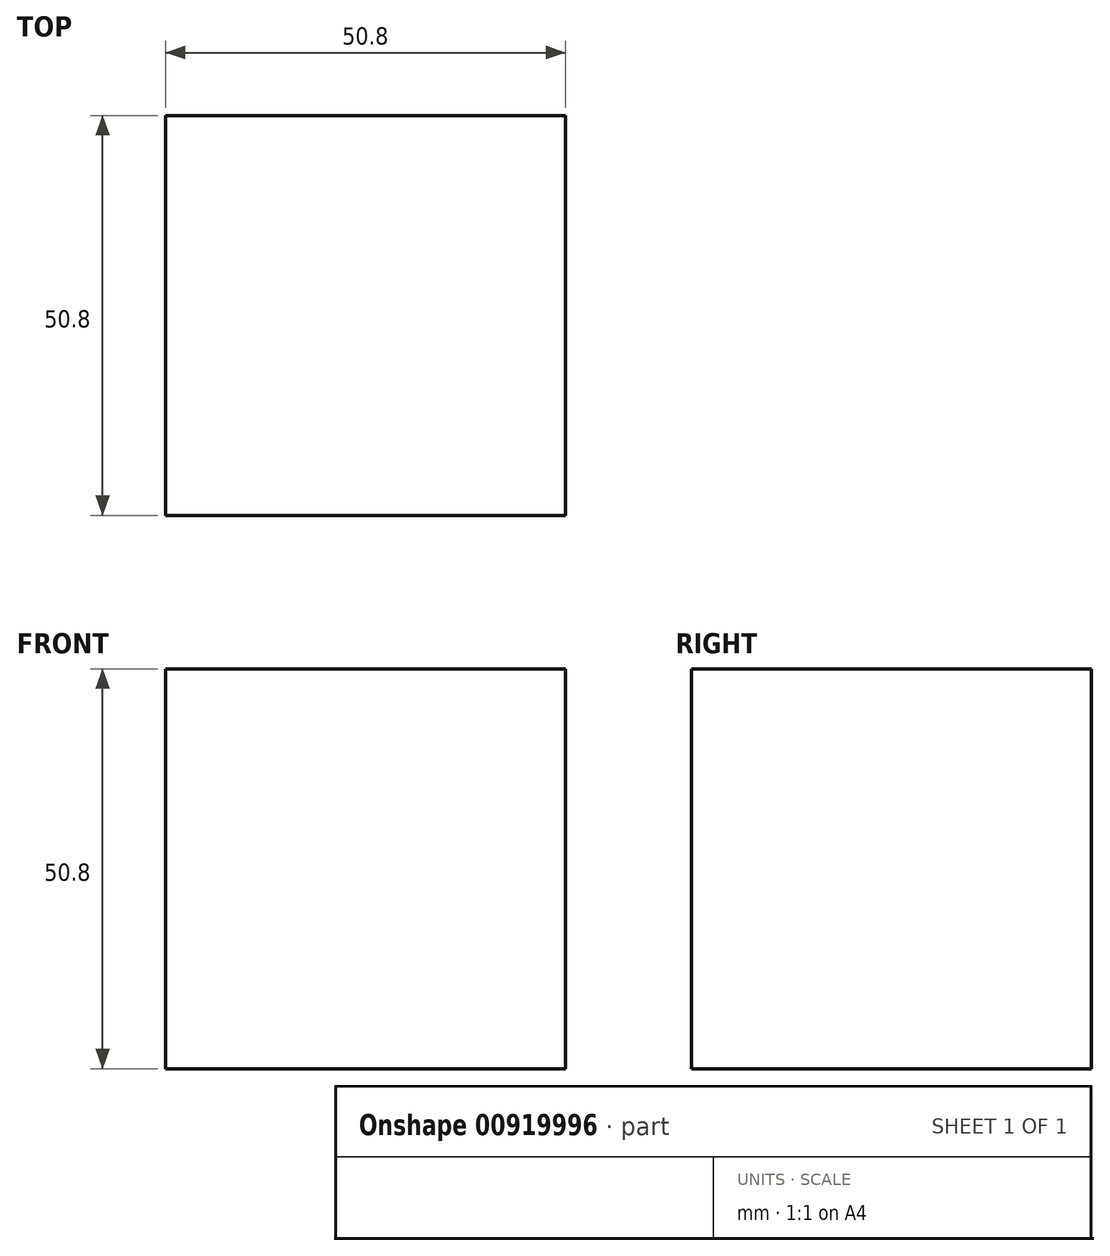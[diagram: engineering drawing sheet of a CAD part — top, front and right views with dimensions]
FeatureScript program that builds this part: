
annotation { "Feature Type Name" : "Feature", "Feature Type Description" : "" }
export const myFeature = defineFeature(function(context is Context, id is Id, definition is map)
    precondition{}
    {
        {
            var Q0;
            Q0=qCreatedBy(makeId("Top.planeOp"),FACE);
            var sketch = newSketch(context, id + "F0", { "sketchPlane" : qUnion([Q0])});
            skLineSegment(sketch, "E0.bottom", {"start": v(-23.76, 20.42) * mm, "end": v(27.04, 20.42) * mm});
            skLineSegment(sketch, "E0.top", {"start": v(-23.76, -30.38) * mm, "end": v(27.04, -30.38) * mm});
            skLineSegment(sketch, "E0.left", {"start": v(-23.76, 20.42) * mm, "end": v(-23.76, -30.38) * mm});
            skLineSegment(sketch, "E0.right", {"start": v(27.04, 20.42) * mm, "end": v(27.04, -30.38) * mm});
            skSolve(sketch);
        }
        {
            var Q0;
            Q0=makeQuery(id+"F0.imprint","IMPRINT",FACE,{"disambiguationData":[TD([[makeQuery(id+"F0.imprint","IMPRINT",EDGE,{"derivedFrom":sQuery(id+"F0.wireOp",EDGE,"E0.bottom")}),-1.0]])]});
            extrude(context, id + "F1", {"entities" : qUnion([Q0]), "depth" : 50.8 * mm, "offsetDistance" : 25.4 * mm});
        }
    });
